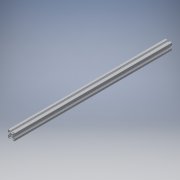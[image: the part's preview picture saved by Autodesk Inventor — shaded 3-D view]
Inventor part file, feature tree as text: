
AUTODESK INVENTOR PART (.ipt)
format: ipt  version: 2016 (Build 200138000, 138)  size: 404,992 bytes
history: native  units: in
note: dims shown in document units (in); Inventor stores cm internally (conversion verified against a paired STEP export)
features: other x3, sketch x2, extrude x1, hole x1, mirror x1
ambient origin geometry x8: Origin, YZ Plane, XZ Plane, XY Plane, X Axis, Y Axis, Z Axis, Center Point
bodies: Solid1 (feature_tree)
feature tree (8):
  other  "Blocks"
  extrude  "Extrusion1"  Depth=2.0in
  hole  "Hole1"  [1 undecoded]
  mirror  "Mirror1"
  sketch  "Sketch1"  dims[d1=0.0in d5=2.0in]
  other  "20x20"
  sketch  "Sketch3"  dims[d6=0.187in d7=0.75in d8=0.375in d9=0.25in d10=0.5635in d11=1.0in d12=0.8108in d13=1.0in d14=1.0in]
  other  "20x20:1"
note: 1 required parameter value undecoded (feature->parameter linkage not recoverable at this tier; creation-order binding heuristic only, values carry confidence <= 0.55)
